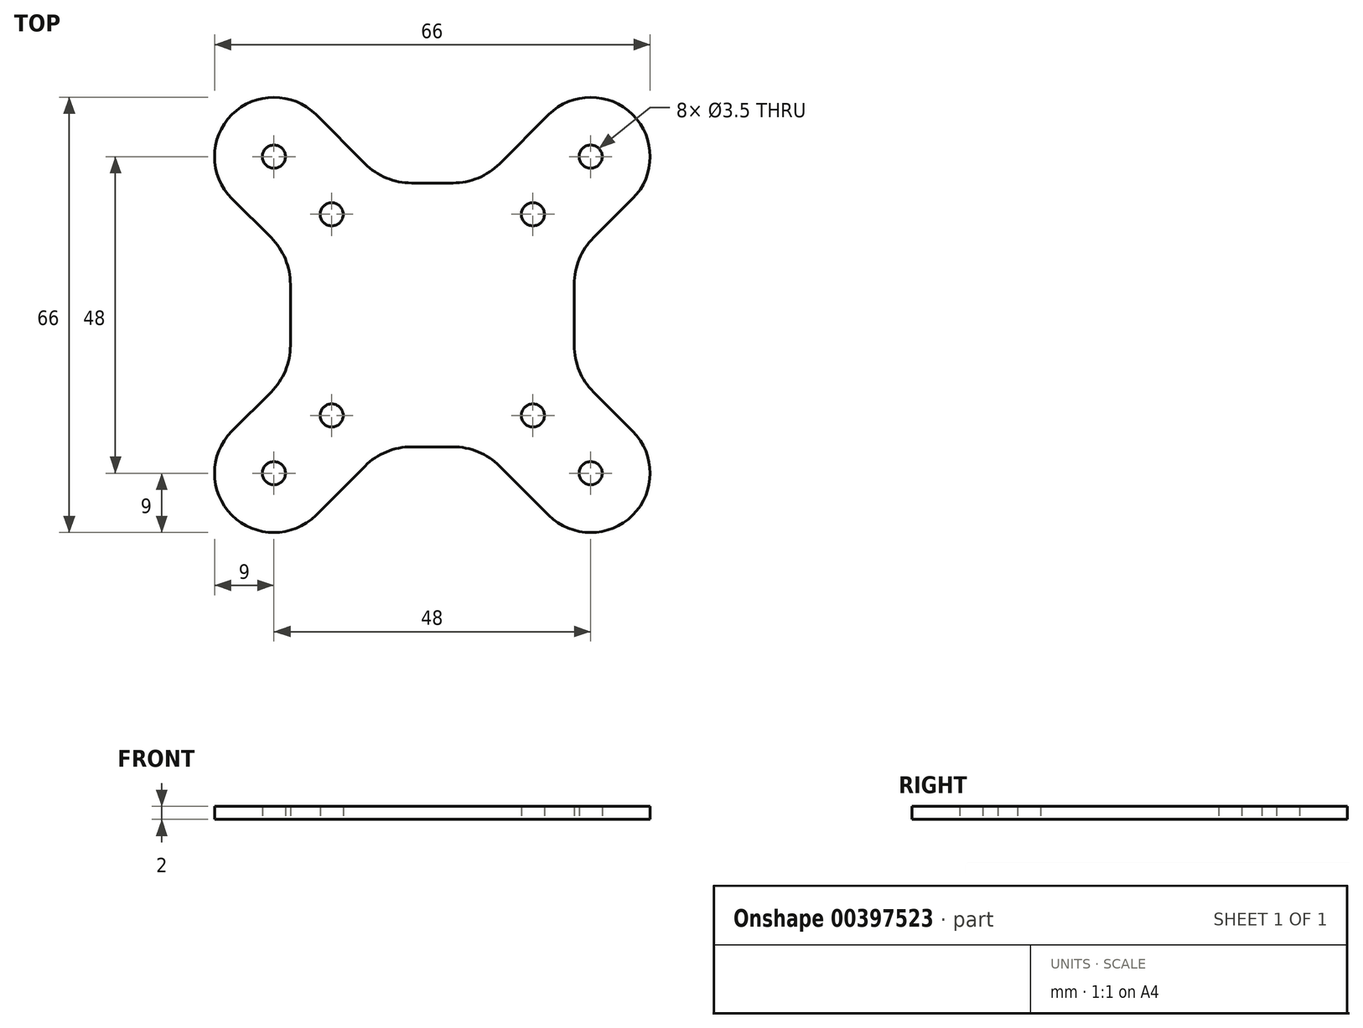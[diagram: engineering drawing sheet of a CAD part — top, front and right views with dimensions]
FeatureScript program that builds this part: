
annotation { "Feature Type Name" : "Feature", "Feature Type Description" : "" }
export const myFeature = defineFeature(function(context is Context, id is Id, definition is map)
    precondition{}
    {
        {
            var Q0;
            Q0=qCreatedBy(makeId("Top.planeOp"),FACE);
            var sketch = newSketch(context, id + "F0", { "sketchPlane" : qUnion([Q0])});
            skCircle(sketch, "E0", {"center": v(-15.25, 15.25) * mm, "radius": 1.75 * mm});
            skCircle(sketch, "E1", {"center": v(-24, 24) * mm, "radius": 1.75 * mm});
            skLineSegment(sketch, "E2", {"start": v(0, 0) * mm, "end": v(-24, 24) * mm, "construction": true});
            skLineSegment(sketch, "E3", {"start": v(-30.36, 17.64) * mm, "end": v(-24.43, 11.7) * mm});
            skLineSegment(sketch, "E4", {"start": v(-17.64, 30.36) * mm, "end": v(-10.2, 22.93) * mm});
            skLineSegment(sketch, "E5", {"start": v(-30.36, 30.36) * mm, "end": v(-30.36, 30.36) * mm});
            skPoint(sketch, "E6.visualSharp", {"position": v(-24, 36.73) * mm});
            skArc(sketch, "E6.filletArc", {"start": v(-17.64, 30.36) * mm, "mid": v(-24, 33) * mm, "end": v(-30.36, 30.36) * mm});
            skPoint(sketch, "E7.visualSharp", {"position": v(-36.73, 24) * mm});
            skArc(sketch, "E7.filletArc", {"start": v(-30.36, 30.36) * mm, "mid": v(-33, 24) * mm, "end": v(-30.36, 17.64) * mm});
            skLineSegment(sketch, "E8", {"start": v(-21.5, 4.63) * mm, "end": v(-21.5, 0) * mm});
            skLineSegment(sketch, "E9", {"start": v(-3.13, 20) * mm, "end": v(0, 20) * mm});
            skPoint(sketch, "E10.visualSharp", {"position": v(-7.27, 20) * mm});
            skArc(sketch, "E10.filletArc", {"start": v(-10.2, 22.93) * mm, "mid": v(-6.96, 20.76) * mm, "end": v(-3.13, 20) * mm});
            skPoint(sketch, "E11.visualSharp", {"position": v(-21.5, 8.77) * mm});
            skArc(sketch, "E11.filletArc", {"start": v(-21.5, 4.63) * mm, "mid": v(-22.26, 8.46) * mm, "end": v(-24.43, 11.7) * mm});
            skPoint(sketch, "E12.MirrorP", {"position": v(36.73, 24) * mm});
            skCircle(sketch, "E13.MirrorC", {"center": v(15.25, 15.25) * mm, "radius": 1.75 * mm});
            skCircle(sketch, "E14.MirrorC", {"center": v(24, 24) * mm, "radius": 1.75 * mm});
            skPoint(sketch, "E15.MirrorP", {"position": v(24, 36.73) * mm});
            skLineSegment(sketch, "E16.MirrorCS", {"start": v(0, 0) * mm, "end": v(24, 24) * mm, "construction": true});
            skPoint(sketch, "E17.MirrorP", {"position": v(7.27, 20) * mm});
            skLineSegment(sketch, "E18.MirrorCS", {"start": v(30.36, 17.64) * mm, "end": v(24.43, 11.7) * mm});
            skLineSegment(sketch, "E19.MirrorCS", {"start": v(17.64, 30.36) * mm, "end": v(10.2, 22.93) * mm});
            skArc(sketch, "E20.MirrorCS", {"start": v(17.64, 30.36) * mm, "mid": v(24, 33) * mm, "end": v(30.36, 30.36) * mm});
            skLineSegment(sketch, "E21.MirrorCS", {"start": v(21.5, 4.63) * mm, "end": v(21.5, 0) * mm});
            skArc(sketch, "E22.MirrorCS", {"start": v(30.36, 30.36) * mm, "mid": v(33, 24) * mm, "end": v(30.36, 17.64) * mm});
            skLineSegment(sketch, "E23.MirrorCS", {"start": v(30.36, 30.36) * mm, "end": v(30.36, 30.36) * mm});
            skArc(sketch, "E24.MirrorCS", {"start": v(21.5, 4.63) * mm, "mid": v(22.26, 8.46) * mm, "end": v(24.43, 11.7) * mm});
            skLineSegment(sketch, "E25.MirrorCS", {"start": v(3.13, 20) * mm, "end": v(0, 20) * mm});
            skPoint(sketch, "E26.MirrorP", {"position": v(21.5, 8.77) * mm});
            skArc(sketch, "E27.MirrorCS", {"start": v(10.2, 22.93) * mm, "mid": v(6.96, 20.76) * mm, "end": v(3.13, 20) * mm});
            skArc(sketch, "E28.MirrorCS", {"start": v(17.64, -30.36) * mm, "mid": v(24, -33) * mm, "end": v(30.36, -30.36) * mm});
            skLineSegment(sketch, "E29.MirrorCS", {"start": v(30.36, -30.36) * mm, "end": v(30.36, -30.36) * mm});
            skArc(sketch, "E30.MirrorCS", {"start": v(30.36, -30.36) * mm, "mid": v(33, -24) * mm, "end": v(30.36, -17.64) * mm});
            skLineSegment(sketch, "E31.MirrorCS", {"start": v(3.13, -20) * mm, "end": v(0, -20) * mm});
            skCircle(sketch, "E32.MirrorC", {"center": v(24, -24) * mm, "radius": 1.75 * mm});
            skCircle(sketch, "E33.MirrorC", {"center": v(15.25, -15.25) * mm, "radius": 1.75 * mm});
            skArc(sketch, "E34.MirrorCS", {"start": v(-21.5, -4.63) * mm, "mid": v(-22.26, -8.46) * mm, "end": v(-24.43, -11.7) * mm});
            skArc(sketch, "E35.MirrorCS", {"start": v(-10.2, -22.93) * mm, "mid": v(-6.96, -20.76) * mm, "end": v(-3.13, -20) * mm});
            skLineSegment(sketch, "E36.MirrorCS", {"start": v(-3.13, -20) * mm, "end": v(0, -20) * mm});
            skLineSegment(sketch, "E37.MirrorCS", {"start": v(-21.5, -4.63) * mm, "end": v(-21.5, 0) * mm});
            skArc(sketch, "E38.MirrorCS", {"start": v(-30.36, -30.36) * mm, "mid": v(-33, -24) * mm, "end": v(-30.36, -17.64) * mm});
            skArc(sketch, "E39.MirrorCS", {"start": v(-17.64, -30.36) * mm, "mid": v(-24, -33) * mm, "end": v(-30.36, -30.36) * mm});
            skLineSegment(sketch, "E40.MirrorCS", {"start": v(-17.64, -30.36) * mm, "end": v(-10.2, -22.93) * mm});
            skPoint(sketch, "E41.MirrorP", {"position": v(7.27, -20) * mm});
            skLineSegment(sketch, "E42.MirrorCS", {"start": v(-30.36, -17.64) * mm, "end": v(-24.43, -11.7) * mm});
            skLineSegment(sketch, "E43.MirrorCS", {"start": v(0, 0) * mm, "end": v(-24, -24) * mm, "construction": true});
            skPoint(sketch, "E44.MirrorP", {"position": v(-24, -36.73) * mm});
            skPoint(sketch, "E45.MirrorP", {"position": v(21.5, -8.77) * mm});
            skLineSegment(sketch, "E46.MirrorCS", {"start": v(17.64, -30.36) * mm, "end": v(10.2, -22.93) * mm});
            skLineSegment(sketch, "E47.MirrorCS", {"start": v(-30.36, -30.36) * mm, "end": v(-30.36, -30.36) * mm});
            skCircle(sketch, "E48.MirrorC", {"center": v(-15.25, -15.25) * mm, "radius": 1.75 * mm});
            skCircle(sketch, "E49.MirrorC", {"center": v(-24, -24) * mm, "radius": 1.75 * mm});
            skPoint(sketch, "E50.MirrorP", {"position": v(36.73, -24) * mm});
            skLineSegment(sketch, "E51.MirrorCS", {"start": v(30.36, -17.64) * mm, "end": v(24.43, -11.7) * mm});
            skLineSegment(sketch, "E52.MirrorCS", {"start": v(0, 0) * mm, "end": v(24, -24) * mm, "construction": true});
            skLineSegment(sketch, "E53.MirrorCS", {"start": v(21.5, -4.63) * mm, "end": v(21.5, 0) * mm});
            skPoint(sketch, "E54.MirrorP", {"position": v(-36.73, -24) * mm});
            skPoint(sketch, "E55.MirrorP", {"position": v(-7.27, -20) * mm});
            skPoint(sketch, "E56.MirrorP", {"position": v(-21.5, -8.77) * mm});
            skArc(sketch, "E57.MirrorCS", {"start": v(21.5, -4.63) * mm, "mid": v(22.26, -8.46) * mm, "end": v(24.43, -11.7) * mm});
            skArc(sketch, "E58.MirrorCS", {"start": v(10.2, -22.93) * mm, "mid": v(6.96, -20.76) * mm, "end": v(3.13, -20) * mm});
            skPoint(sketch, "E59.MirrorP", {"position": v(24, -36.73) * mm});
            skSolve(sketch);
        }
        {
            var Q0;
            Q0=makeQuery(id+"F0.imprint","IMPRINT",FACE,{"disambiguationData":[TD([[makeQuery(id+"F0.imprint","IMPRINT",EDGE,{"derivedFrom":sQuery(id+"F0.wireOp",EDGE,"E0")}),-1.0]])]});
            extrude(context, id + "F1", {"entities" : qUnion([Q0]), "depth" : 2 * mm});
        }
    });
